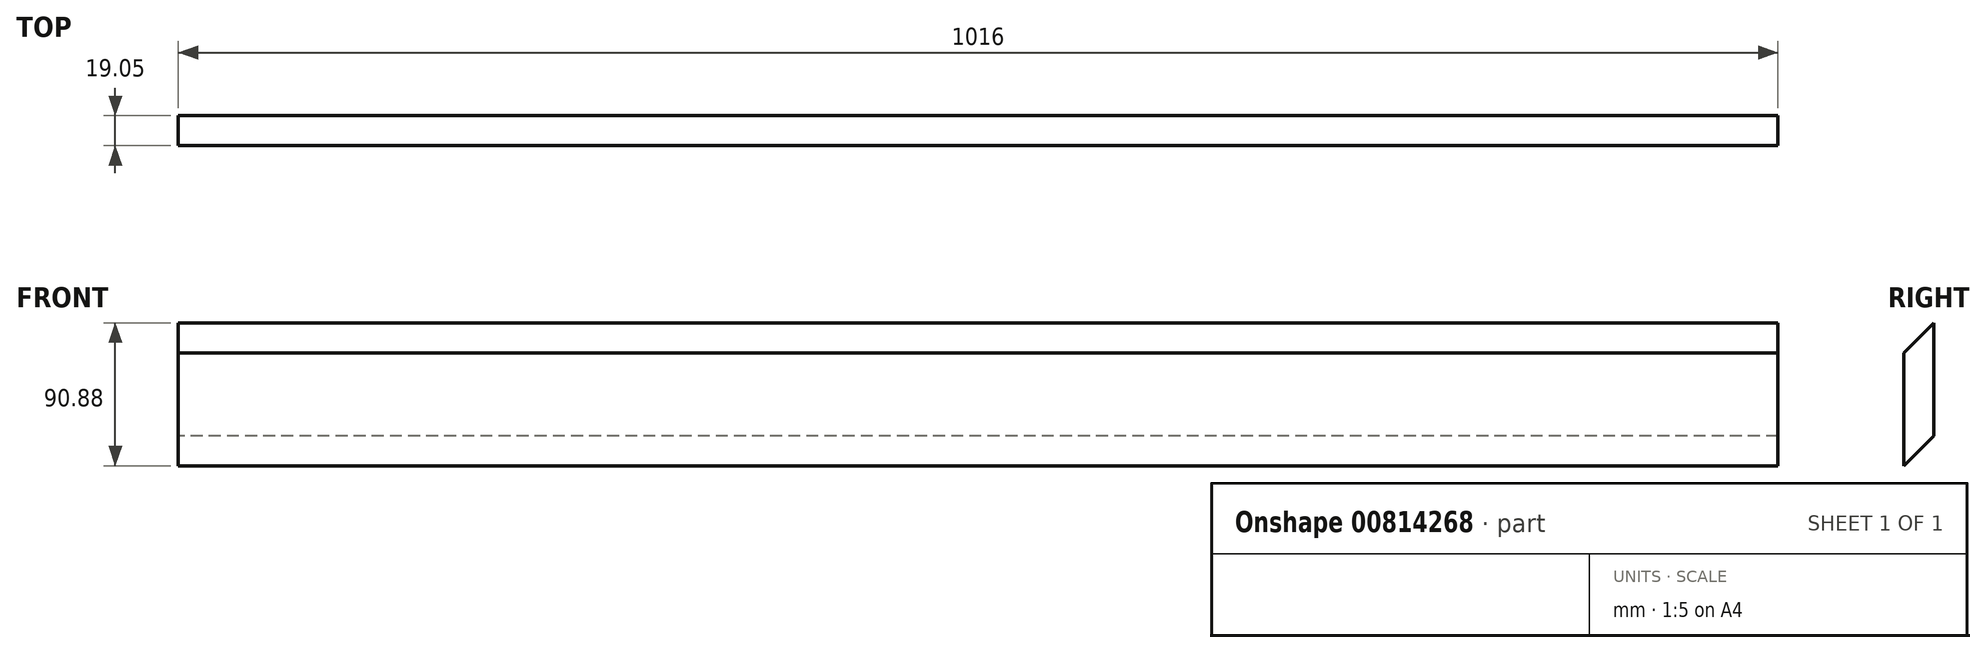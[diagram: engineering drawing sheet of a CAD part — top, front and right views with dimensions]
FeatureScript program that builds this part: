
annotation { "Feature Type Name" : "Feature", "Feature Type Description" : "" }
export const myFeature = defineFeature(function(context is Context, id is Id, definition is map)
    precondition{}
    {
        {
            var Q0;
            Q0=qCreatedBy(makeId("Right.planeOp"),FACE);
            var sketch = newSketch(context, id + "F0", { "sketchPlane" : qUnion([Q0])});
            skLineSegment(sketch, "E0", {"start": v(-19.05, 0) * mm, "end": v(0, 19.05) * mm});
            skLineSegment(sketch, "E1", {"start": v(0, 19.05) * mm, "end": v(0, 90.88) * mm});
            skLineSegment(sketch, "E2", {"start": v(0, 90.88) * mm, "end": v(-19.05, 71.83) * mm});
            skLineSegment(sketch, "E3", {"start": v(-19.05, 71.83) * mm, "end": v(-19.05, 0) * mm});
            skSolve(sketch);
        }
        {
            var Q0;
            Q0 = qSketchRegion(id + "F0", true);
            extrude(context, id + "F1", {"entities" : qUnion([Q0]), "endBound" : BoundingType.SYMMETRIC, "depth" : 1016 * mm, "offsetDistance" : 25.4 * mm});
        }
    });
